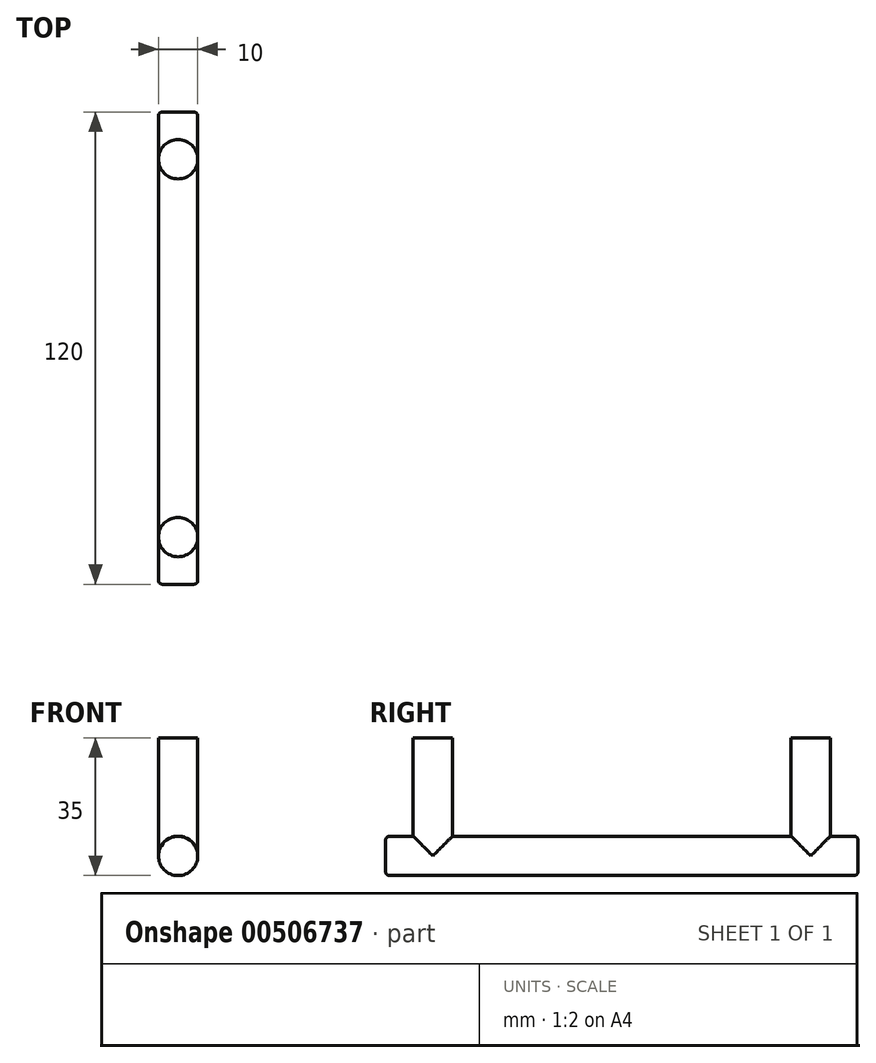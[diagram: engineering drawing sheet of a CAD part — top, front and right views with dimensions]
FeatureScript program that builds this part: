
annotation { "Feature Type Name" : "Feature", "Feature Type Description" : "" }
export const myFeature = defineFeature(function(context is Context, id is Id, definition is map)
    precondition{}
    {
        {
            var Q0;
            Q0=qCreatedBy(makeId("Front.planeOp"),FACE);
            var sketch = newSketch(context, id + "F0", { "sketchPlane" : qUnion([Q0])});
            skCircle(sketch, "E0", {"center": v(0, 0) * mm, "radius": 5 * mm});
            skSolve(sketch);
        }
        {
            var Q0;
            Q0=qSketchRegion(id+"F0",true);
            extrude(context, id + "F1", {"entities" : qUnion([Q0]), "endBound" : BoundingType.SYMMETRIC, "depth" : 120 * mm});
        }
        {
            var Q0;
            Q0=qCreatedBy(makeId("Top.planeOp"),FACE);
            var sketch = newSketch(context, id + "F2", { "sketchPlane" : qUnion([Q0])});
            skCircle(sketch, "E1", {"center": v(0, 48) * mm, "radius": 5 * mm});
            skCircle(sketch, "E2", {"center": v(0, -48) * mm, "radius": 5 * mm});
            skSolve(sketch);
        }
        {
            var Q0;
            Q0=qSketchRegion(id+"F2",true);
            extrude(context, id + "F3", {"entities" : qUnion([Q0]), "operationType" : NewBodyOperationType.ADD, "depth" : 30 * mm});
        }
        {
            var Q0;
            Q0=makeQuery(id+"F1.opExtrude","CAP_EDGE",EDGE,{"disambiguationData":[OSD([sQuery(id+"F0.wireOp",EDGE,"E0")])],"isStart":true});
            var Q1;
            Q1=makeQuery(id+"F1.opExtrude","CAP_EDGE",EDGE,{"disambiguationData":[OSD([sQuery(id+"F0.wireOp",EDGE,"E0")])],"isStart":false});
            fillet(context, id + "F4", {"entities" : qUnion([Q0, Q1]), "radius" : 1 * mm, "tangentPropagation" : true, "allowEdgeOverflow" : false});
        }
    });
